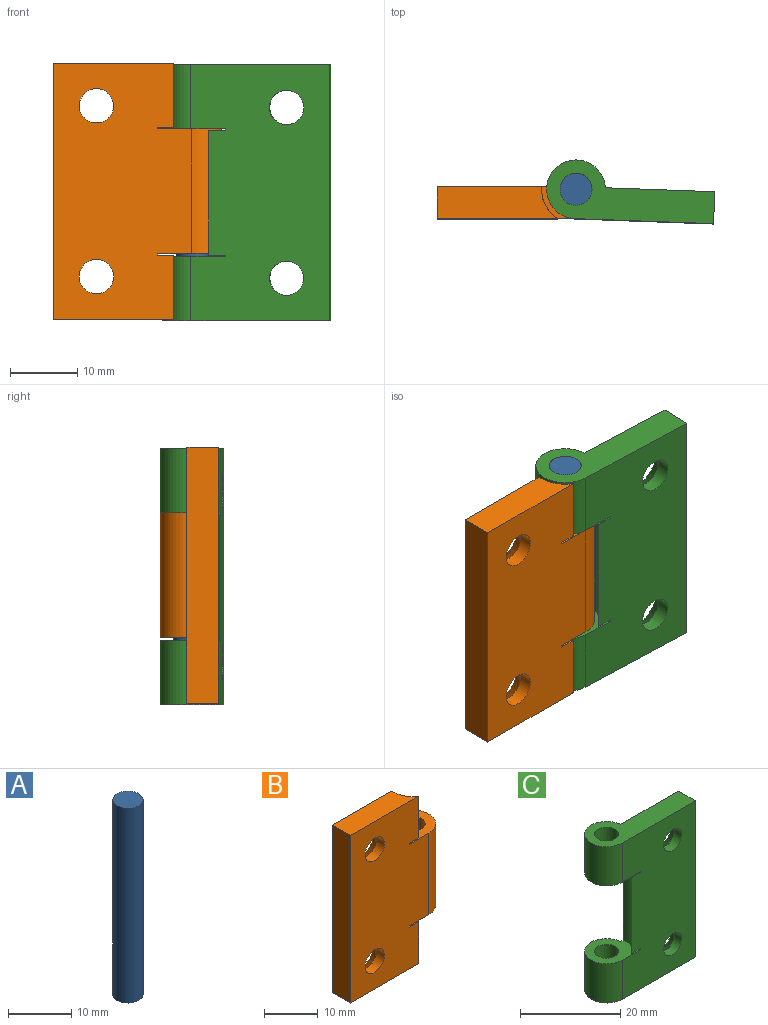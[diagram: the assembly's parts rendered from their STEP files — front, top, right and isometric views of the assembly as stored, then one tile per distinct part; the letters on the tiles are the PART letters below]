
ASSEMBLY  parts=3 mates=2
PART A: 3 faces, bbox 4.8x4.8x37.6 mm
  f0: cylinder r=2.38mm len=37.59mm, axis (0,0,-1), area 562.4mm2, adj f1,f2
  f1: plane 4.76x4.76mm, normal (0,0,1), area 17.8mm2, adj f0
  f2: plane 4.76x4.76mm, normal (0,0,-1), area 17.8mm2, adj f0
PART B: 21 faces, bbox 25x8.7x38.1 mm
  f0: cylinder r=2.55mm len=5.11mm, axis (0,1,0), area 33.1mm2, adj f1,f6
  f1: cone r=4.89mm half-angle=41deg, axis (0,1,0), area 83.3mm2, adj f0,f7
  f2: cylinder r=2.55mm len=5.11mm, axis (0,1,0), area 33.1mm2, adj f3,f6
  f3: cone r=4.89mm half-angle=41deg, axis (0,1,0), area 83.3mm2, adj f2,f7
  f4: cylinder r=5.13mm len=9.53mm, axis (0,0,-1), area 53.4mm2, adj f6,f7,f10,f11,f16
  f5: cylinder r=2.38mm len=18.54mm, axis (0,0,-1), area 277.4mm2, adj f17,f20
  f6: plane 38.1x20.64mm, normal (0,-1,0), area 691.6mm2, adj f0,f2,f4,f8,f11,f12,f13,f14
  f7: plane 38.1x16.29mm, normal (0,1,0), area 455.5mm2, adj f1,f3,f4,f8,f11,f12,f13,f14
  f8: cylinder r=4.37mm len=18.54mm, axis (0,0,-1), area 374.3mm2, adj f6,f7,f17,f20
  f9: plane 0.77x0.01mm, normal (0,0,1), area 0mm2, adj f14,f18
  f10: plane 0.77x0.01mm, normal (0,0,-1), area 0mm2, adj f4,f15
  f11: plane 17.95x4.75mm, normal (0,0,-1), area 76.8mm2, adj f4,f6,f7,f13
  f12: plane 17.95x4.75mm, normal (0,0,1), area 76.8mm2, adj f6,f7,f13,f14
  f13: plane 38.1x4.75mm, normal (-1,0,0), area 181mm2, adj f6,f7,f11,f12
  f14: cylinder r=5.13mm len=9.53mm, axis (0,0,1), area 53.4mm2, adj f6,f7,f9,f12,f19
  f15: plane 4.75x0.25mm, normal (1,0,0), area 1.2mm2, adj f6,f7,f10,f16,f17
  f16: plane 3.98x2.43mm, normal (0,0,1), area 3.1mm2, adj f4,f6,f15
  f17: plane 9.48x8.73mm, normal (0,0,-1), area 49.7mm2, adj f5,f6,f7,f8,f15
  f18: plane 4.75x0.25mm, normal (1,0,0), area 1.2mm2, adj f6,f7,f9,f19,f20
  f19: plane 3.98x2.43mm, normal (0,0,-1), area 3.1mm2, adj f6,f14,f18
  f20: plane 9.48x8.73mm, normal (0,0,1), area 49.7mm2, adj f5,f6,f7,f8,f18
PART C: 20 faces, bbox 25x8.7x38.1 mm
  f0: cylinder r=2.55mm len=5.11mm, axis (0,1,0), area 33.1mm2, adj f1,f16
  f1: cone r=4.89mm half-angle=41deg, axis (0,1,0), area 83.3mm2, adj f0,f14
  f2: cylinder r=2.55mm len=5.11mm, axis (0,1,0), area 33.1mm2, adj f3,f16
  f3: cone r=4.89mm half-angle=41deg, axis (0,1,0), area 83.3mm2, adj f2,f14
  f4: cylinder r=2.38mm len=9.53mm, axis (0,0,-1), area 142.5mm2, adj f15,f17
  f5: cylinder r=5.13mm len=19.05mm, axis (0,0,1), area 104.4mm2, adj f11,f12,f13,f14,f15,f16,f18,f19
  f6: cylinder r=4.37mm len=9.53mm, axis (0,0,-1), area 192.3mm2, adj f14,f15,f16,f17
  f7: cylinder r=4.37mm len=9.53mm, axis (0,0,-1), area 192.3mm2, adj f10,f13,f14,f16
  f8: cylinder r=2.38mm len=9.53mm, axis (0,0,-1), area 142.5mm2, adj f10,f13
  f9: plane 38.1x4.75mm, normal (1,0,0), area 181mm2, adj f10,f14,f16,f17
  f10: plane 25x8.73mm, normal (0,0,-1), area 123.4mm2, adj f7,f8,f9,f14,f16
  f11: plane 3.98x2.43mm, normal (0,0,-1), area 3.1mm2, adj f5,f12,f16
  f12: plane 3.98x0.25mm, normal (-1,0,0), area 1mm2, adj f5,f11,f13,f16
  f13: plane 9.49x8.73mm, normal (0,0,1), area 49.7mm2, adj f5,f7,f8,f12,f14,f16
  f14: plane 38.1x16.29mm, normal (0,1,0), area 455.9mm2, adj f1,f3,f5,f6,f7,f9,f10,f13
  f15: plane 9.49x8.73mm, normal (0,0,-1), area 49.7mm2, adj f4,f5,f6,f14,f16,f19
  f16: plane 38.1x20.64mm, normal (0,-1,0), area 693mm2, adj f0,f2,f5,f6,f7,f9,f10,f11
  f17: plane 25x8.73mm, normal (0,0,1), area 123.4mm2, adj f4,f6,f9,f14,f16
  f18: plane 3.98x2.43mm, normal (0,0,1), area 3.1mm2, adj f5,f16,f19
  f19: plane 3.98x0.25mm, normal (-1,0,0), area 1mm2, adj f5,f15,f16,f18
PLACE A t=(-6.35,-9.96,4.16)mm
PLACE B t=(-6.35,-9.96,4.16)mm fixed
PLACE C rot(axis=(0,0,-1),2.1deg) t=(-6.51,-9.96,3.9)mm
MATE revolute C.f4 <-> A.f0  axis (0,0,1) through (-6.35,-5.6,22.95)mm
MATE fastened A.f0 <-> B.f4  axis (0,0,-1) through (-6.35,-5.6,4.16)mm
